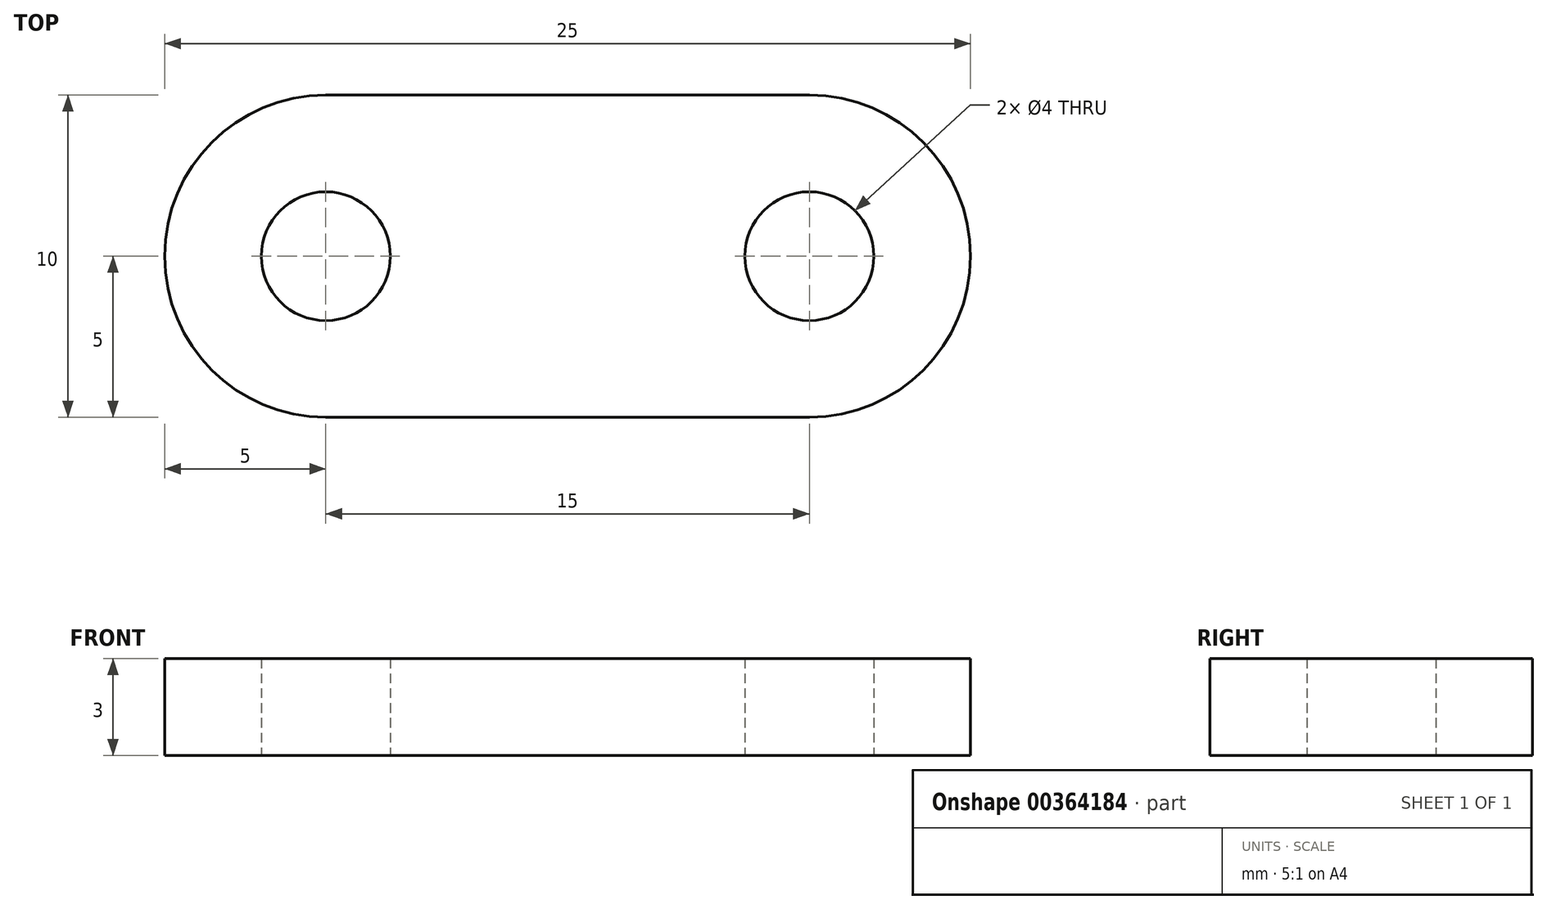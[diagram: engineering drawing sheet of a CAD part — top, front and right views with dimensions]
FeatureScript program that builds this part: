
annotation { "Feature Type Name" : "Feature", "Feature Type Description" : "" }
export const myFeature = defineFeature(function(context is Context, id is Id, definition is map)
    precondition{}
    {
        {
            var Q0;
            Q0=qCreatedBy(makeId("Top.planeOp"),FACE);
            var sketch = newSketch(context, id + "F0", { "sketchPlane" : qUnion([Q0])});
            skLineSegment(sketch, "E0.bottom", {"start": v(7.5, 5) * mm, "end": v(-7.5, 5) * mm});
            skLineSegment(sketch, "E0.top", {"start": v(7.5, -5) * mm, "end": v(-7.5, -5) * mm});
            skPoint(sketch, "E0.middle", {"position": v(0, 0) * mm});
            skCircle(sketch, "E1", {"center": v(-7.5, 0) * mm, "radius": 2 * mm});
            skCircle(sketch, "E2", {"center": v(7.5, 0) * mm, "radius": 2 * mm});
            skArc(sketch, "E3", {"start": v(-7.5, 5) * mm, "mid": v(-12.5, 0) * mm, "end": v(-7.5, -5) * mm});
            skArc(sketch, "E4", {"start": v(7.5, -5) * mm, "mid": v(12.5, 0) * mm, "end": v(7.5, 5) * mm});
            skSolve(sketch);
        }
        {
            var Q0;
            Q0=qSketchRegion(id+"F0",true);
            extrude(context, id + "F1", {"entities" : qUnion([Q0]), "depth" : 3 * mm});
        }
    });
